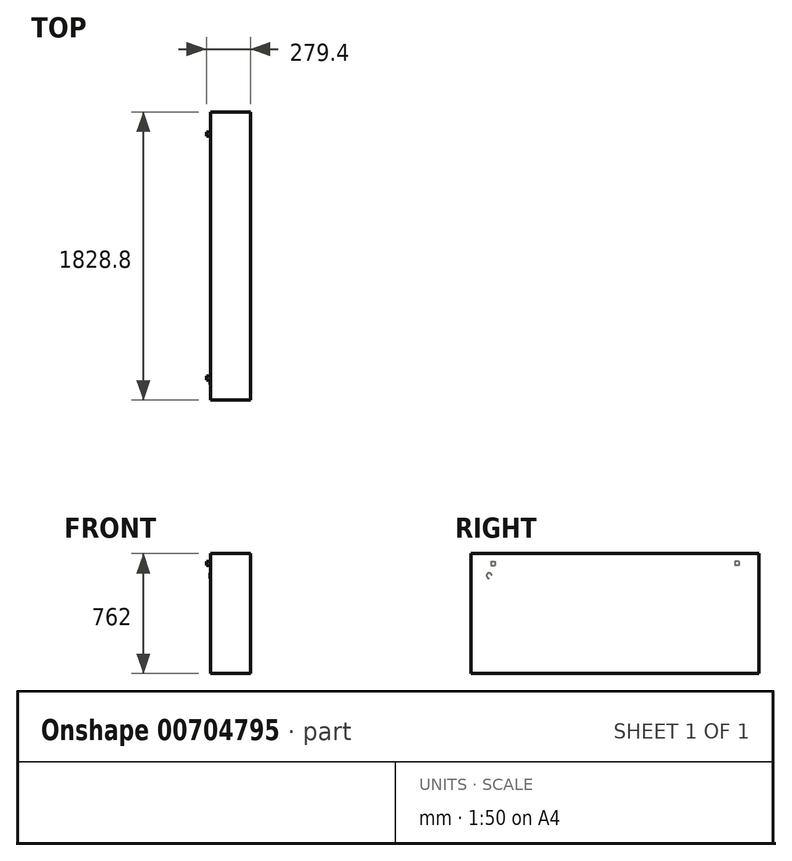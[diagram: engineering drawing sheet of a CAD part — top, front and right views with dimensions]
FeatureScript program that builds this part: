
annotation { "Feature Type Name" : "Feature", "Feature Type Description" : "" }
export const myFeature = defineFeature(function(context is Context, id is Id, definition is map)
    precondition{}
    {
        {
            var Q0;
            Q0=qCreatedBy(makeId("Front.planeOp"),FACE);
            var sketch = newSketch(context, id + "F0", { "sketchPlane" : qUnion([Q0])});
            skLineSegment(sketch, "E0.bottom", {"start": v(-127, -381) * mm, "end": v(127, -381) * mm});
            skLineSegment(sketch, "E0.top", {"start": v(-127, 381) * mm, "end": v(127, 381) * mm});
            skLineSegment(sketch, "E0.left", {"start": v(-127, -381) * mm, "end": v(-127, 381) * mm});
            skLineSegment(sketch, "E0.right", {"start": v(127, -381) * mm, "end": v(127, 381) * mm});
            skPoint(sketch, "E0.middle", {"position": v(0, 0) * mm});
            skSolve(sketch);
        }
        {
            var Q0;
            Q0 = qSketchRegion(id + "F0", true);
            extrude(context, id + "F1", {"entities" : qUnion([Q0]), "depth" : 1828.8 * mm, "offsetDistance" : 25.4 * mm});
        }
        {
            var Q0;
            Q0=makeQuery(id+"F1.opExtrude","SWEPT_FACE",FACE,{"disambiguationData":[OSD([sQuery(id+"F0.wireOp",EDGE,"E0.left")])]});
            var sketch = newSketch(context, id + "F2", { "sketchPlane" : qUnion([Q0])});
            skLineSegment(sketch, "E1.bottom", {"start": v(1701.8, 330.2) * mm, "end": v(1676.4, 330.2) * mm});
            skLineSegment(sketch, "E1.top", {"start": v(1701.8, 304.8) * mm, "end": v(1676.4, 304.8) * mm});
            skLineSegment(sketch, "E1.left", {"start": v(1701.8, 330.2) * mm, "end": v(1701.8, 304.8) * mm});
            skLineSegment(sketch, "E1.right", {"start": v(1676.4, 330.2) * mm, "end": v(1676.4, 304.8) * mm});
            skLineSegment(sketch, "E2.bottom", {"start": v(127, 330.2) * mm, "end": v(152.4, 330.2) * mm});
            skLineSegment(sketch, "E2.top", {"start": v(127, 304.8) * mm, "end": v(152.4, 304.8) * mm});
            skLineSegment(sketch, "E2.left", {"start": v(127, 330.2) * mm, "end": v(127, 304.8) * mm});
            skLineSegment(sketch, "E2.right", {"start": v(152.4, 330.2) * mm, "end": v(152.4, 304.8) * mm});
            skSolve(sketch);
        }
        {
            var Q0;
            Q0 = qSketchRegion(id + "F2", true);
            extrude(context, id + "F3", {"entities" : qUnion([Q0]), "operationType" : NewBodyOperationType.ADD, "depth" : 25.4 * mm, "offsetDistance" : 25.4 * mm});
        }
        {
            var Q0;
            Q0=makeQuery(id+"F1.opExtrude","SWEPT_FACE",FACE,{"disambiguationData":[OSD([sQuery(id+"F0.wireOp",EDGE,"E0.left")])]});
            var sketch = newSketch(context, id + "F4", { "sketchPlane" : qUnion([Q0])});
            skCircle(sketch, "E3", {"center": v(1714.52, 240.17) * mm, "radius": 16.47 * mm});
            skSolve(sketch);
        }
        {
            var Q0;
            Q0 = qSketchRegion(id + "F4", true);
            extrude(context, id + "F5", {"entities" : qUnion([Q0]), "operationType" : NewBodyOperationType.ADD, "depth" : 2.54 * mm, "offsetDistance" : 25.4 * mm});
        }
        {
            var Q0;
            Q0=makeQuery(id+"F5.opExtrude","CAP_EDGE",EDGE,{"disambiguationData":[OSD([sQuery(id+"F4.wireOp",EDGE,"E3")])],"isStart":false});
            fillet(context, id + "F6", {"entities" : qUnion([Q0]), "radius" : 5.08 * mm, "tangentPropagation" : true, "allowEdgeOverflow" : false});
        }
    });
